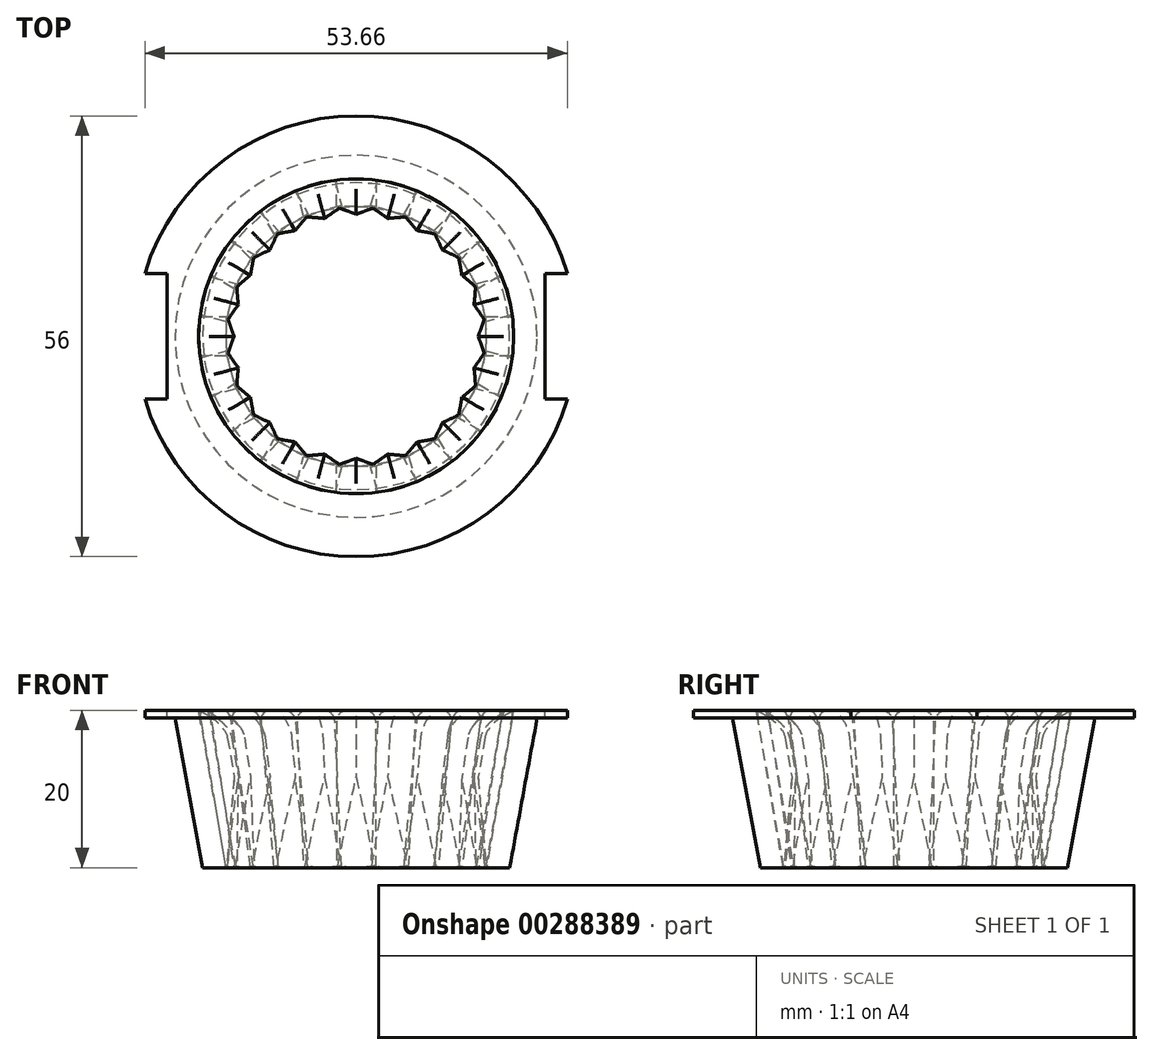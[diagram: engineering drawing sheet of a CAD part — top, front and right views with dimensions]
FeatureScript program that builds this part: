
annotation { "Feature Type Name" : "Feature", "Feature Type Description" : "" }
export const myFeature = defineFeature(function(context is Context, id is Id, definition is map)
    precondition{}
    {
        {
            var Q0;
            Q0=qCreatedBy(makeId("Front.planeOp"),FACE);
            var sketch = newSketch(context, id + "F0", { "sketchPlane" : qUnion([Q0])});
            skLineSegment(sketch, "E0", {"start": v(-43.53, 0) * mm, "end": v(19.5, 0) * mm, "construction": true});
            skLineSegment(sketch, "E1", {"start": v(16.5, 0) * mm, "end": v(19.5, 0) * mm});
            skLineSegment(sketch, "E2", {"start": v(0, 23.67) * mm, "end": v(0, -27.14) * mm, "construction": true});
            skLineSegment(sketch, "E3", {"start": v(20, 20) * mm, "end": v(0, 20) * mm, "construction": true});
            skLineSegment(sketch, "E4", {"start": v(16.5, 0) * mm, "end": v(20, 20) * mm});
            skLineSegment(sketch, "E5", {"start": v(20, 20) * mm, "end": v(28, 20) * mm});
            skLineSegment(sketch, "E6", {"start": v(28, 20) * mm, "end": v(28, 19) * mm});
            skLineSegment(sketch, "E7", {"start": v(28, 19) * mm, "end": v(23, 19) * mm});
            skLineSegment(sketch, "E8", {"start": v(23, 19) * mm, "end": v(19.5, 0) * mm});
            skSolve(sketch);
        }
        {
            var Q0;
            Q0 = qSketchRegion(id + "F0", true);
            var Q1;
            Q1=sQuery(id+"F0.wireOp",EDGE,"E2");
            revolve(context, id + "F1", {"entities" : qUnion([Q0]), "axis" : qUnion([Q1]), "revolveType" : RevolveType.FULL});
        }
        {
            var Q0;
            Q0=makeQuery(id+"F1.opRevolve","SWEPT_FACE",FACE,{"disambiguationData":[OSD([sQuery(id+"F0.wireOp",EDGE,"E5")])]});
            var sketch = newSketch(context, id + "F2", { "sketchPlane" : qUnion([Q0])});
            skLineSegment(sketch, "E9", {"start": v(-28.21, 0) * mm, "end": v(29.27, 0) * mm, "construction": true});
            skCircle(sketch, "E10.0", {"center": v(0, 0) * mm, "radius": 28 * mm, "construction": true});
            skLineSegment(sketch, "E11", {"start": v(-24, 0) * mm, "end": v(-24, 8) * mm});
            skLineSegment(sketch, "E12", {"start": v(-24, 8) * mm, "end": v(-26.83, 8) * mm});
            skLineSegment(sketch, "E13.MirrorCS", {"start": v(-24, 0) * mm, "end": v(-24, -8) * mm});
            skLineSegment(sketch, "E14.MirrorCS", {"start": v(-24, -8) * mm, "end": v(-26.83, -8) * mm});
            skLineSegment(sketch, "E15.MirrorCS", {"start": v(24, 0) * mm, "end": v(24, -8) * mm});
            skLineSegment(sketch, "E16.MirrorCS", {"start": v(24, -8) * mm, "end": v(26.83, -8) * mm});
            skLineSegment(sketch, "E17.MirrorCS", {"start": v(24, 8) * mm, "end": v(26.83, 8) * mm});
            skLineSegment(sketch, "E18.MirrorCS", {"start": v(24, 0) * mm, "end": v(24, 8) * mm});
            skSolve(sketch);
        }
        {
            var Q0;
            Q0=makeQuery(id+"F2.imprint","IMPRINT",FACE,{"disambiguationData":[TD([[makeQuery(id+"F2.imprint","IMPRINT",EDGE,{"derivedFrom":sQuery(id+"F2.wireOp",EDGE,"E11")}),1.0]])]});
            var Q1;
            Q1=makeQuery(id+"F2.imprint","IMPRINT",FACE,{"disambiguationData":[TD([[makeQuery(id+"F2.imprint","IMPRINT",EDGE,{"derivedFrom":sQuery(id+"F2.wireOp",EDGE,"E15.MirrorCS")}),1.0]])]});
            extrude(context, id + "F3", {"entities" : qUnion([Q0, Q1]), "operationType" : NewBodyOperationType.REMOVE, "oppositeDirection" : true, "depth" : 2 * mm});
        }
        {
            var Q0;
            Q0=qCreatedBy(makeId("Front.planeOp"),FACE);
            var sketch = newSketch(context, id + "F4", { "sketchPlane" : qUnion([Q0])});
            skLineSegment(sketch, "E19", {"start": v(-20, 20) * mm, "end": v(-16.5, 0) * mm});
            skLineSegment(sketch, "E20", {"start": v(0, 23.38) * mm, "end": v(0, -4.9) * mm, "construction": true});
            skSolve(sketch);
        }
        {
            var Q0;
            Q0=sQuery(id+"F4.wireOp",EDGE,"E19");
            cPlane(context, id + "F5", {"entities" : qUnion([Q0]), "cplaneType" : CPlaneType.LINE_ANGLE, "offset" : 25 * mm, "angle" : 0 * degree, "width" : 150 * mm, "height" : 150 * mm});
        }
        {
            var Q0;
            Q0=qCreatedBy(id+"F5.planeOp",FACE);
            var sketch = newSketch(context, id + "F6", { "sketchPlane" : qUnion([Q0])});
            skLineSegment(sketch, "E21.bottom", {"start": v(2.5, 2.84) * mm, "end": v(-2.5, 2.84) * mm});
            skLineSegment(sketch, "E21.top", {"start": v(2.5, 23.15) * mm, "end": v(-2.5, 23.15) * mm});
            skLineSegment(sketch, "E21.left", {"start": v(2.5, 2.84) * mm, "end": v(2.5, 23.15) * mm});
            skLineSegment(sketch, "E21.right", {"start": v(-2.5, 2.84) * mm, "end": v(-2.5, 23.15) * mm});
            skPoint(sketch, "E21.middle", {"position": v(0, 13) * mm});
            skSolve(sketch);
        }
        {
            var Q0;
            Q0=makeQuery(id+"F6.imprint","IMPRINT",FACE,{"disambiguationData":[TD([[makeQuery(id+"F6.imprint","IMPRINT",EDGE,{"derivedFrom":sQuery(id+"F6.wireOp",EDGE,"E21.bottom")}),-1.0]])]});
            extrude(context, id + "F7", {"entities" : qUnion([Q0]), "oppositeDirection" : true, "depth" : 3 * mm, "hasDraft" : true, "draftAngle" : 40 * degree, "draftPullDirection" : true});
        }
        {
            var Q0;
            Q0=makeQuery(id+"F7.opExtrude","SWEPT_EDGE",EDGE,{"disambiguationData":[OSD([sQuery(id+"F6.wireOp",EDGE,"E21.top"),sQuery(id+"F6.wireOp",EDGE,"E21.right")])]});
            var Q1;
            Q1=makeQuery(id+"F7.opExtrude","SWEPT_EDGE",EDGE,{"disambiguationData":[OSD([sQuery(id+"F6.wireOp",EDGE,"E21.top"),sQuery(id+"F6.wireOp",EDGE,"E21.left")])]});
            fillet(context, id + "F8", {"entities" : qUnion([Q0, Q1]), "radius" : 2 * mm, "tangentPropagation" : true, "allowEdgeOverflow" : false});
        }
        {
            var Q0;
            Q0=makeQuery(id+"F7.opExtrude","SWEPT_BODY",BODY,{"disambiguationData":[OSD([sQuery(id+"F6.wireOp",EDGE,"E21.bottom"),sQuery(id+"F6.wireOp",EDGE,"E21.top"),sQuery(id+"F6.wireOp",EDGE,"E21.left"),sQuery(id+"F6.wireOp",EDGE,"E21.right")])]});
            var Q1;
            Q1=sQuery(id+"F4.wireOp",EDGE,"E20");
            circularPattern(context, id + "F9", {"entities" : qUnion([Q0]), "axis" : qUnion([Q1]), "angle" : 360 * degree, "instanceCount" : 24, "equalSpace" : true, "computeTransformsWithoutBuiltin" : true});
        }
        {
            var Q0;
            Q0=makeQuery(id+"F1.opRevolve","SWEPT_FACE",FACE,{"disambiguationData":[OSD([sQuery(id+"F0.wireOp",EDGE,"E1")])]});
            var sketch = newSketch(context, id + "F10", { "sketchPlane" : qUnion([Q0])});
            skCircle(sketch, "E22.0", {"center": v(0, 0) * mm, "radius": 16.5 * mm});
            skSolve(sketch);
        }
        {
            var Q0;
            Q0=makeQuery(id+"F10.imprint","IMPRINT",FACE,{"disambiguationData":[TD([[makeQuery(id+"F10.imprint","IMPRINT",EDGE,{"derivedFrom":sQuery(id+"F10.wireOp",EDGE,"E22.0")}),-1.0]])]});
            extrude(context, id + "F11", {"entities" : qUnion([Q0]), "operationType" : NewBodyOperationType.REMOVE, "oppositeDirection" : true, "depth" : 15 * mm, "hasDraft" : true, "draftAngle" : 5 * degree, "draftPullDirection" : true});
        }
    });
